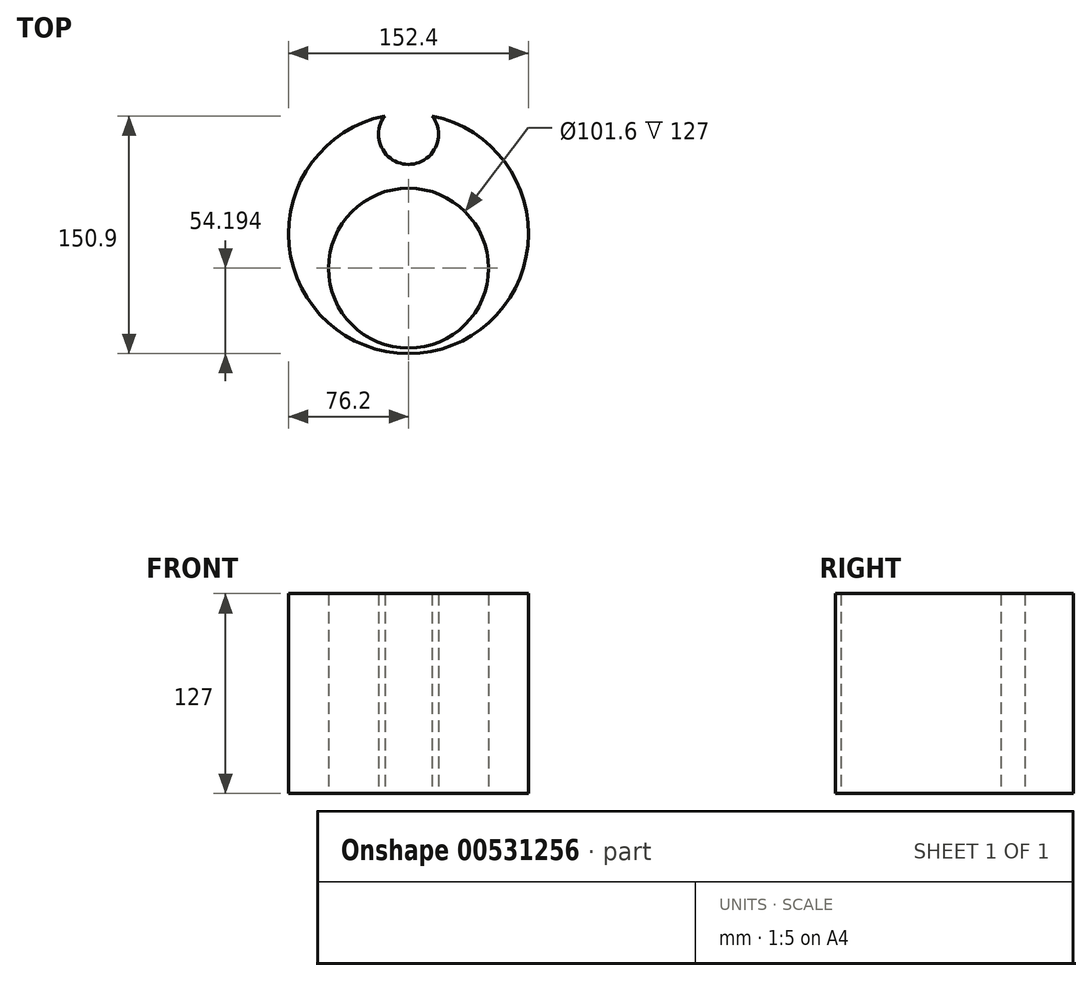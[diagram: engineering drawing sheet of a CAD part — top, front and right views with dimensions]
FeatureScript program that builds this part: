
annotation { "Feature Type Name" : "Feature", "Feature Type Description" : "" }
export const myFeature = defineFeature(function(context is Context, id is Id, definition is map)
    precondition{}
    {
        {
            var Q0;
            Q0=qCreatedBy(makeId("Top.planeOp"),FACE);
            var sketch = newSketch(context, id + "F0", { "sketchPlane" : qUnion([Q0])});
            skCircle(sketch, "E0", {"center": v(0, 0) * mm, "radius": 76.2 * mm});
            skCircle(sketch, "E1", {"center": v(0, 63) * mm, "radius": 19.05 * mm});
            skCircle(sketch, "E2", {"center": v(0, -22) * mm, "radius": 50.8 * mm});
            skSolve(sketch);
        }
        {
            var Q0;
            Q0=makeQuery(id+"F0.imprint","IMPRINT",FACE,{"disambiguationData":[TD([[makeQuery(id+"F0.imprint","IMPRINT",EDGE,{"derivedFrom":sQuery(id+"F0.wireOp",EDGE,"E2")}),-1.0]])]});
            extrude(context, id + "F1", {"entities" : qUnion([Q0]), "depth" : 127 * mm, "offsetDistance" : 25.4 * mm});
        }
    });
